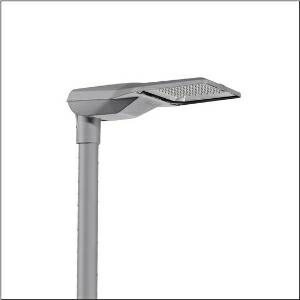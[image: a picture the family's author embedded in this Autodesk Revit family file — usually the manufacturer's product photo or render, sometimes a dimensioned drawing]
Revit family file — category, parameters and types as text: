
# Revit family: streetlight_sl_21_midi___st0_8a_5xe7c63a08lb_8ff2
name_source: partatom
category: Lighting Fixtures
units: mm (PartAtom-declared; Revit-internal decimal feet)

## family parameters
Cut with Voids When Loaded = No
Host = Face
Light Source = No
Part Type = Normal
Room Calculation Point = No
Round Connector Dimension = Use Diameter
Shared = No

## types (1)
- --- (1 x LED, 12860 lm, 98.3 W, 2700K)
    Apparent Load = 98 VA
    CIE Flux Codes = 38 75 97 100 100
    Color Rendering = 70
    Color Temperature = 2700K
    Default Elevation = 1800 mm
    Description = Streetlight SL 21 midi, mast luminaire, primary light control with lens, of PMMA, primary optical cover: cover, of toughened safety glass, transparent, light distribution: ST0.8a, light emission: direct distribution, primary light characteristic: asymmetric, installation type: post-top, side-entry, LED, 3G 1.5mm², High Power LED, rated luminous flux: 12.860lm, luminous efficacy: 131lm/W, light colour: 727, colour temperature: 2700K, control gear: Easy, control: overheat protection, constant luminous flux control, time-dependent luminous flux control, flexible luminous flux parameterisation, mains connection: 220..240V, AC, 50/60Hz, connection cable pre-assembled, cable length: 10,5m, wiring characteristics: H07RN-F, start of lifetime: 98W, end of service life: 101W, reduction: 44W, luminaire housing, of diecast aluminium, powder-coated, Siteco® metallic grey (DB 702S), corrosivity category C5 mid according to DIN EN ISO 12944, please order mast flange separately, inclination adjustable: 0°, 5°, 10°, 15°, sealing non-destructively replaceable, multi-level sealing system, length: 644mm, width: 335mm, height: 110mm, mast flange for spigot size: 42mm (side-entry): 5XC10008XM4, 60/48mm (side-entry/post-top): 5XC10108XM2, 76/60mm (side-entry/post-top): 5XC10108XM1, mounting height: 4..8m, protection rating (complete): IP66, insulation class (complete): insulation class II (safety insulation), certification: CE, ENEC, ENEC+, VDE, impact resistance: IK10, permissible operating ambient temperature for outdoor applications: -40..+50°C, standard-compliant lighting for roads and squares, packaging unit: 1 piece

Light Distribution: ST0.8a
    Height = 111 mm
    Lamp = 1 x LED
    Lamp Light Flux = 12860 lm
    Lamp Power = 98.3 W
    Lamp count = 1
    Length = 644 mm
    Luminous efficacy = 131 lm/W
    Manufacturer = Siteco
    ModVariant = No
    Model = 5XE7C63A08LB
    Number of Poles = 1
    OnlyDefault = Yes
    Power Factor = 1
    Product Name = Streetlight SL 21 midi | ST0.8a
    Product group = mast luminaire | pylon top
    ProductGroupID = 6100
    Protection Class = Protection class II
    Protection Degree = IP 66
    RLX_Detail_Level = 1
    RLX_Emergency_Light_Flux = 0 lm
    RLX_Emergency_Type = 0
    RLX_Emergency_Type_DB = No
    RlxData = <blob elided: 26901 chars, md5=7504a9aa>
    Socket = socket
    Standby Power = 0 W
    System Light Flux = 12860 lm
    System Power = 98 W
    Type Comments = factory setting: luminous flux: 100 % | Output Level: 100 % | 1020 mA
    Type Image = l_1004298.jpg
    URL = http://relux.com
    VarID = @adj_207131
    Voltage = 0 V
    Weight = 0.00 kg
    Width = 336 mm

## geometry (parser evidence)
native form markers: Blend x4, Sweep x11
no freeform markers — native parametric forms only
